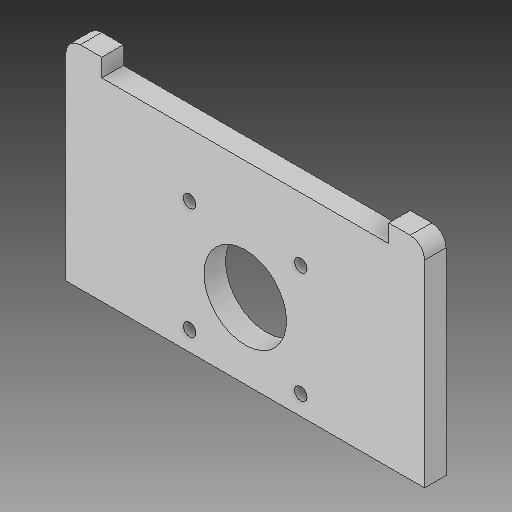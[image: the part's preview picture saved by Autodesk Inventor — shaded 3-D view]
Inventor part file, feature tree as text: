
AUTODESK INVENTOR PART (.ipt)
format: ipt  version: 2019 (Build 230136000, 136)  size: 125,440 bytes
history: native  units: mm
features: extrude x1, fillet x1
ambient origin geometry x8: Origin, YZ Plane, XZ Plane, XY Plane, X Axis, Y Axis, Z Axis, Center Point
bodies: Body1 (feature_tree)
feature tree (2):
  extrude  "Extrusion2"  Depth=100.0mm
  fillet  "Fillet3"  Radius=3.5mm
